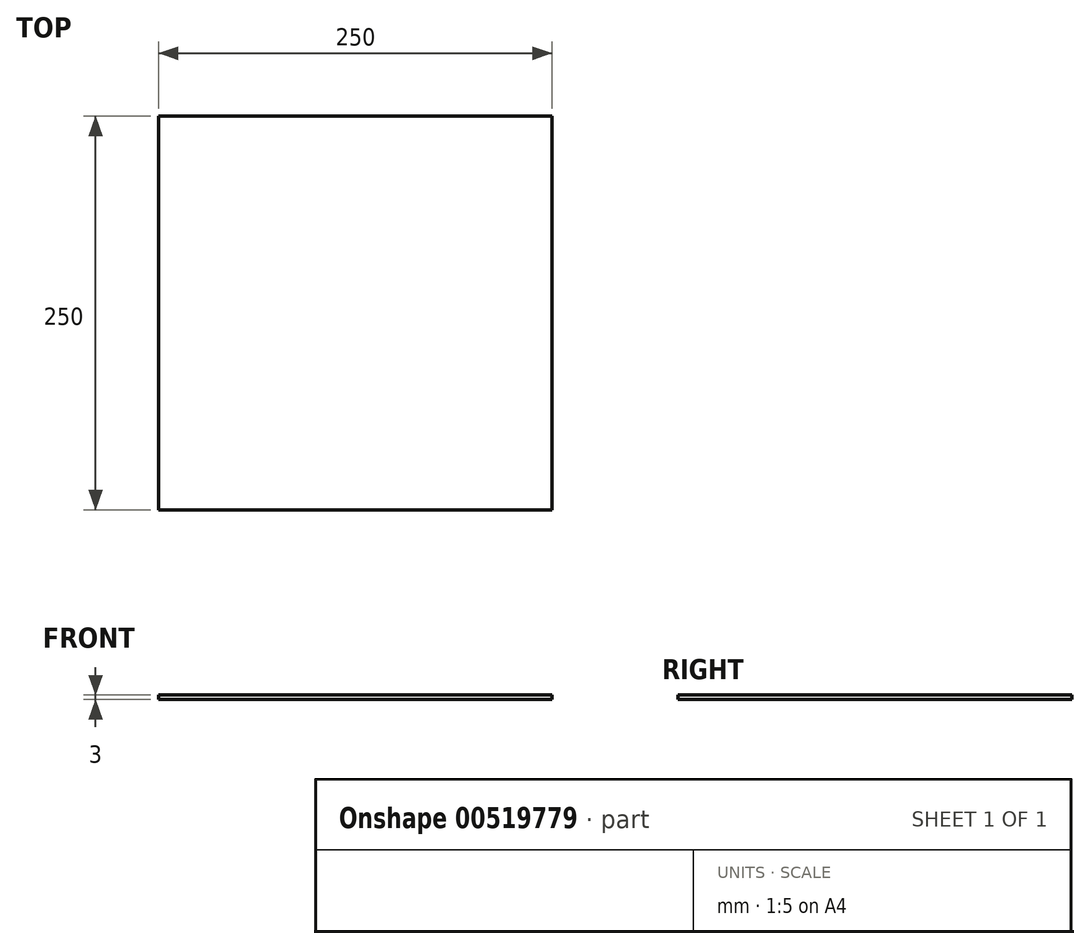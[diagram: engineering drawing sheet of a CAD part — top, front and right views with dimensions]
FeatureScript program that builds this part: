
annotation { "Feature Type Name" : "Feature", "Feature Type Description" : "" }
export const myFeature = defineFeature(function(context is Context, id is Id, definition is map)
    precondition{}
    {
        {
            var Q0;
            Q0=qCreatedBy(makeId("Top.planeOp"),FACE);
            var sketch = newSketch(context, id + "F0", { "sketchPlane" : qUnion([Q0])});
            skLineSegment(sketch, "E0.bottom", {"start": v(2.87, 0) * mm, "end": v(252.87, 0) * mm});
            skLineSegment(sketch, "E0.top", {"start": v(2.87, 250) * mm, "end": v(252.87, 250) * mm});
            skLineSegment(sketch, "E0.left", {"start": v(2.87, 0) * mm, "end": v(2.87, 250) * mm});
            skLineSegment(sketch, "E0.right", {"start": v(252.87, 0) * mm, "end": v(252.87, 250) * mm});
            skSolve(sketch);
        }
        {
            var Q0;
            Q0 = qSketchRegion(id + "F0", true);
            extrude(context, id + "F1", {"entities" : qUnion([Q0]), "depth" : 3 * mm, "offsetDistance" : 25 * mm});
        }
    });
